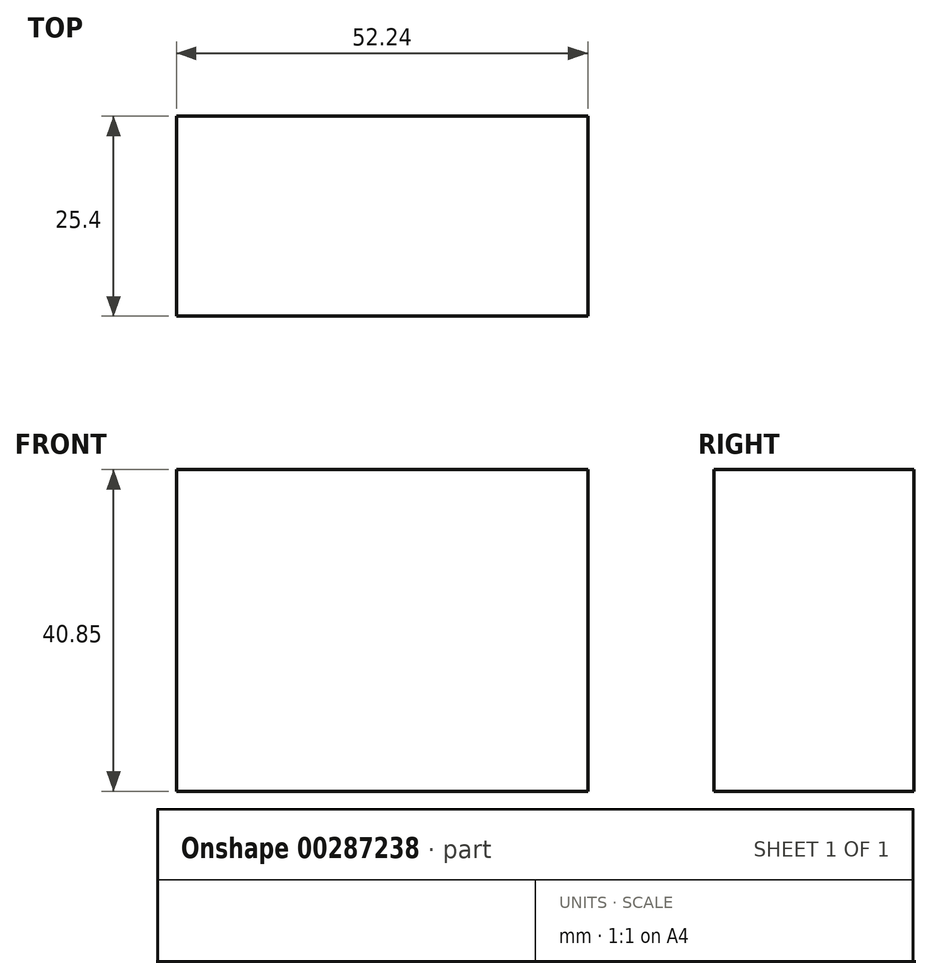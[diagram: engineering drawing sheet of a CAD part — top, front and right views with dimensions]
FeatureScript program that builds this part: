
annotation { "Feature Type Name" : "Feature", "Feature Type Description" : "" }
export const myFeature = defineFeature(function(context is Context, id is Id, definition is map)
    precondition{}
    {
        {
            var Q0;
            Q0=qCreatedBy(makeId("Front.planeOp"),FACE);
            var sketch = newSketch(context, id + "F0", { "sketchPlane" : qUnion([Q0])});
            skLineSegment(sketch, "E0.bottom", {"start": v(0, 0) * mm, "end": v(-52.24, 0) * mm});
            skLineSegment(sketch, "E0.top", {"start": v(0, 40.85) * mm, "end": v(-52.24, 40.85) * mm});
            skLineSegment(sketch, "E0.left", {"start": v(0, 0) * mm, "end": v(0, 40.85) * mm});
            skLineSegment(sketch, "E0.right", {"start": v(-52.24, 0) * mm, "end": v(-52.24, 40.85) * mm});
            skSolve(sketch);
        }
        {
            var Q0;
            Q0 = qSketchRegion(id + "F0", true);
            extrude(context, id + "F1", {"entities" : qUnion([Q0]), "depth" : 25.4 * mm});
        }
    });
